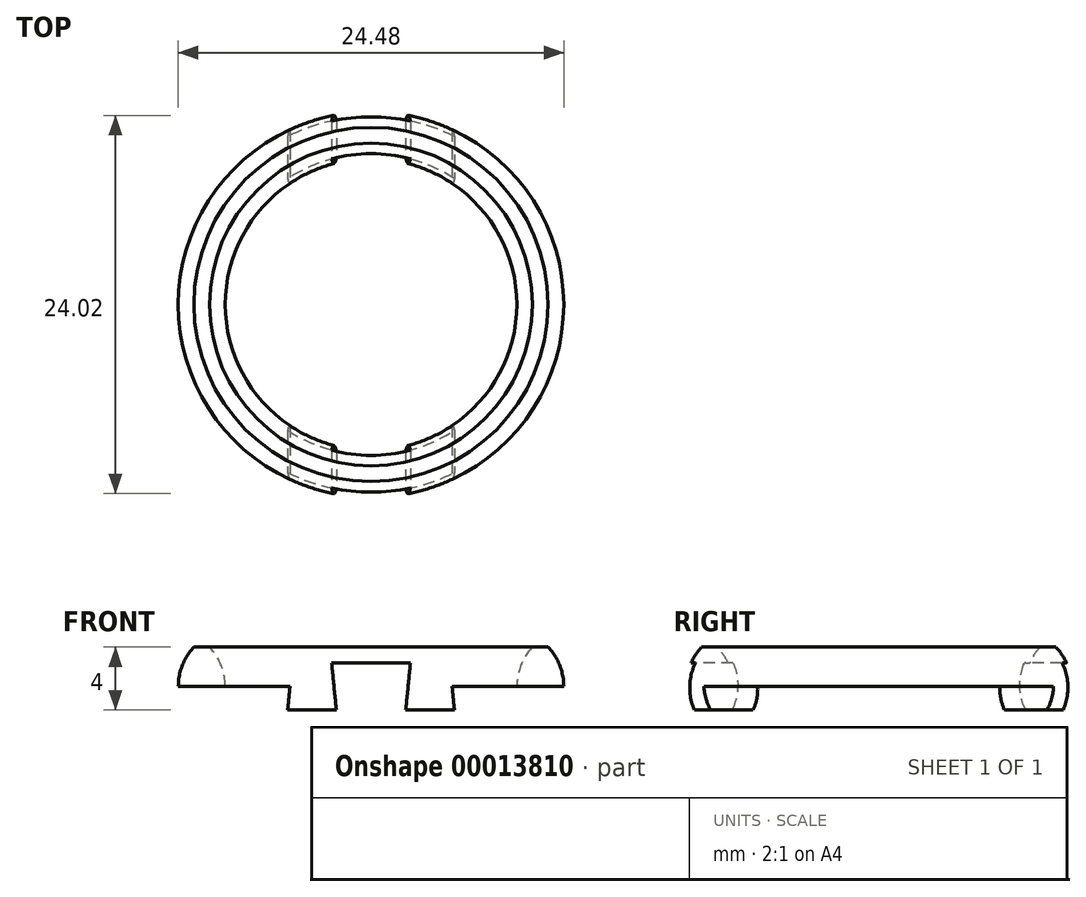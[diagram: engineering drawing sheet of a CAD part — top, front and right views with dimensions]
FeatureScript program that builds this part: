
annotation { "Feature Type Name" : "Feature", "Feature Type Description" : "" }
export const myFeature = defineFeature(function(context is Context, id is Id, definition is map)
    precondition{}
    {
        {
            var Q0;
            Q0=qCreatedBy(makeId("Front.planeOp"),FACE);
            var sketch = newSketch(context, id + "F0", { "sketchPlane" : qUnion([Q0])});
            skLineSegment(sketch, "E0", {"start": v(0, 0) * mm, "end": v(0, 5) * mm});
            skArc(sketch, "E1", {"start": v(-10.25, 0) * mm, "mid": v(-9.26, 2.5) * mm, "end": v(-10.25, 5) * mm});
            skLineSegment(sketch, "E2", {"start": v(-11.25, 5) * mm, "end": v(-10.25, 5) * mm});
            skLineSegment(sketch, "E3", {"start": v(-11.25, 0) * mm, "end": v(-10.25, 0) * mm});
            skArc(sketch, "E4", {"start": v(-11.25, 5) * mm, "mid": v(-12.24, 2.5) * mm, "end": v(-11.25, 0) * mm});
            skPoint(sketch, "E5.orphan", {"position": v(-12.25, 5) * mm});
            skPoint(sketch, "E6.orphan", {"position": v(-12.25, 0) * mm});
            skSolve(sketch);
        }
        {
            var Q0;
            Q0=qSketchRegion(id+"F0",true);
            var Q1;
            Q1=sQuery(id+"F0.wireOp",EDGE,"E0");
            revolve(context, id + "F1", {"entities" : qUnion([Q0]), "axis" : qUnion([Q1]), "revolveType" : RevolveType.FULL});
        }
        {
            var Q0;
            Q0=qCreatedBy(makeId("Front.planeOp"),FACE);
            var sketch = newSketch(context, id + "F2", { "sketchPlane" : qUnion([Q0])});
            skLineSegment(sketch, "E7", {"start": v(-12.26, 2.5) * mm, "end": v(-5.15, 2.5) * mm});
            skLineSegment(sketch, "E8", {"start": v(0, 0) * mm, "end": v(0, 4.5) * mm});
            skLineSegment(sketch, "E9", {"start": v(0, 2.5) * mm, "end": v(0, 3.83) * mm});
            skLineSegment(sketch, "E10", {"start": v(0, 2.5) * mm, "end": v(0, 3.47) * mm});
            skLineSegment(sketch, "E11", {"start": v(0, 2.5) * mm, "end": v(0, 4.5) * mm});
            skLineSegment(sketch, "E12", {"start": v(-2.5, 4) * mm, "end": v(-2.2, 1) * mm});
            skLineSegment(sketch, "E13.0", {"start": v(-5.3, 1) * mm, "end": v(-2.2, 1) * mm});
            skLineSegment(sketch, "E14.0.MirrorCS", {"start": v(-5.15, 2.5) * mm, "end": v(-5.3, 1) * mm});
            skLineSegment(sketch, "E15.trimOffspring", {"start": v(-2.5, 4) * mm, "end": v(0, 4) * mm});
            skLineSegment(sketch, "E16.0.MirrorCS", {"start": v(12.26, 2.5) * mm, "end": v(5.15, 2.5) * mm});
            skLineSegment(sketch, "E17.0.MirrorCS", {"start": v(5.15, 2.5) * mm, "end": v(5.3, 1) * mm});
            skLineSegment(sketch, "E18.0.MirrorCS", {"start": v(5.3, 1) * mm, "end": v(2.2, 1) * mm});
            skLineSegment(sketch, "E19.0.MirrorCS", {"start": v(2.5, 4) * mm, "end": v(2.2, 1) * mm});
            skLineSegment(sketch, "E20.0.MirrorCS", {"start": v(2.5, 4) * mm, "end": v(0, 4) * mm});
            skLineSegment(sketch, "E21", {"start": v(-12.26, -0.9) * mm, "end": v(12.26, -0.9) * mm});
            skLineSegment(sketch, "E22", {"start": v(-12.26, 2.5) * mm, "end": v(-12.26, -0.9) * mm});
            skLineSegment(sketch, "E23", {"start": v(12.26, 2.5) * mm, "end": v(12.26, -0.9) * mm});
            skPoint(sketch, "E24.orphan", {"position": v(-12.26, 5.63) * mm});
            skPoint(sketch, "E25.0.MirrorCS.end.orphan", {"position": v(12.26, 5.63) * mm});
            skPoint(sketch, "E26.0.MirrorCS.end.orphan", {"position": v(6.1, 2.5) * mm});
            skPoint(sketch, "E27.0.MirrorCS.start.orphan", {"position": v(6.25, 4) * mm});
            skPoint(sketch, "E28.orphan", {"position": v(5, 4) * mm});
            skPoint(sketch, "E29.0.end.orphan", {"position": v(-5, 4) * mm});
            skPoint(sketch, "E30.0.MirrorCS.end.orphan", {"position": v(-6.1, 2.5) * mm});
            skPoint(sketch, "E30.0.MirrorCS.start.orphan", {"position": v(-6.25, 4) * mm});
            skSolve(sketch);
        }
        {
            var Q0;
            Q0 = qSketchRegion(id + "F2", true);
            extrude(context, id + "F3", {"entities" : qUnion([Q0]), "operationType" : NewBodyOperationType.REMOVE, "endBound" : BoundingType.SYMMETRIC, "oppositeDirection" : true, "depth" : 25 * mm});
        }
    });
